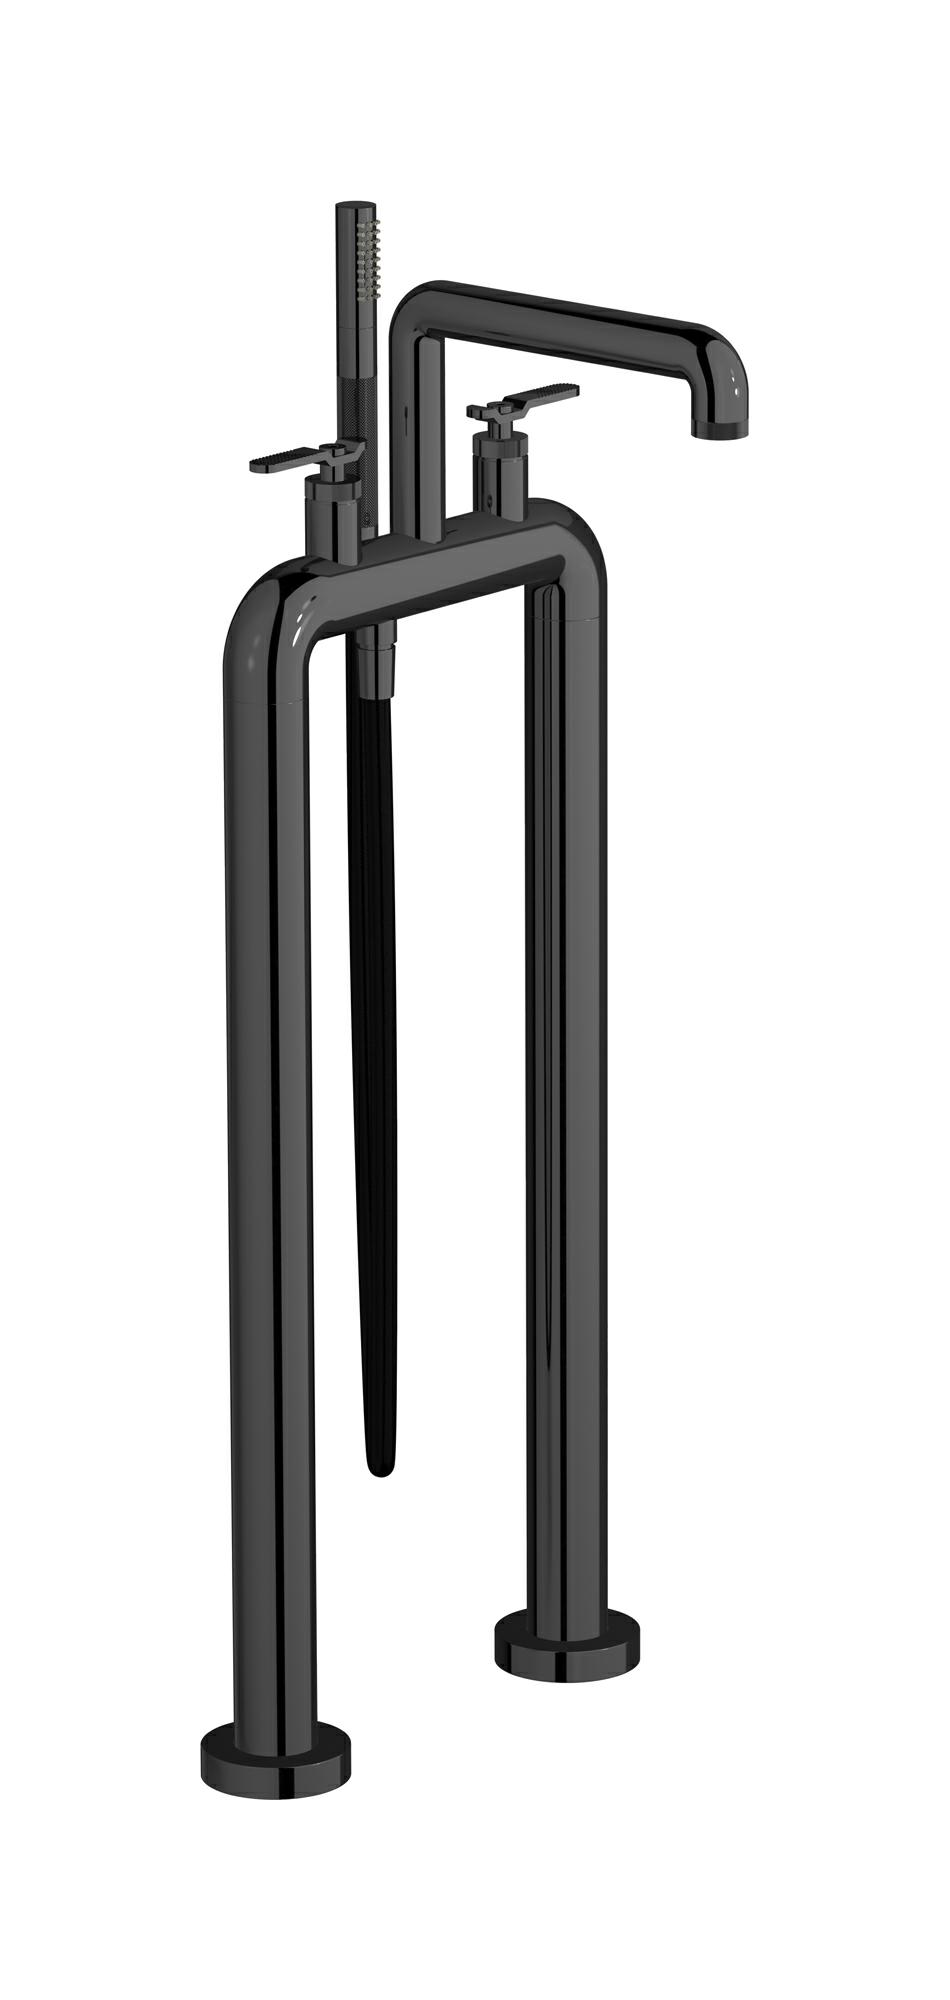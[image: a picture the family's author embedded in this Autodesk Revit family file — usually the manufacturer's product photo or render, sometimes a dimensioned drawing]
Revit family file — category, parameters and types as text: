
# Revit family: B2700
name_source: partatom
category: Apparecchi idraulici
units: mm (PartAtom-declared; Revit-internal decimal feet)

## family parameters
Basato su piano di lavoro = No
Condiviso = No
Mantieni orientamento annotazione = No
Numero OmniClass = 23.45.55.17
Punto di calcolo locali = No
Quota connettore circolare = Usa diametro
Sempre verticale = Sì
Taglio con vuoti quando caricato = No
Tipo di parte = Normale
Titolo OmniClass = Mixing Faucets

## types (13) — shared parameters
Cold water inlet = 10 mm  [stored 0.0328084 ft]
Commenti sul tipo = Freestanding two columns bath filler with shower kit
Connessione CW = No
Connessione HW = No
Connessione di scarico = No
Connessione di ventilazione = No
Descrizione = Freestanding two columns bath filler with shower kit
Hot water inlet = 10 mm  [stored 0.0328084 ft]
Produttore = IB Rubinetterie S.p.A.
URL = https://www.weareib.it
zero-valued in all types: Prospetto di default

## per-type parameters (varying)
| type | Finishes surface | Immagine tipo | Modello |
| Chrome | IB_Chrome | B2700CC.jpg | B2700CC |
| Black Chrome | IB_Black chrome | B2700CF.jpg | B2700CF |
| Brushed Black Chrome | IB_Brushed black chrome | B2700CS.jpg | B2700CS |
| Pale Gold | IB_Pale gold | B2700II.jpg | B2700II |
| Brushed Pale Gold | IB_brushed pale gold | B2700IS.jpg | B2700IS |
| Modern Bronze | IB_Modern bronze | B2700MB.jpg | B2700MB |
| Matt Black | IB_matt black | B2700NP.jpg | B2700NP |
| Natural Brass | IB_Brass | B2700ON.jpg | B2700ON |
| Gold | IB_gold | B2700OO.jpg | B2700OO |
| Brushed Gold | IB_brushed gold | B2700OS.jpg | B2700OS |
| Rose Gold | IB_Rose gold | B2700RS.jpg | B2700RS |
| Brushed Rose Gold | IB_Brushed rose gold | B2700SR.jpg | B2700SR |
| Brushed Nickel | IB_Brushed nickel | B2700SS.jpg | B2700SS |

note: [stored X ft] marks values corroborated as IEEE doubles in the binary element streams (Revit-internal decimal feet)
